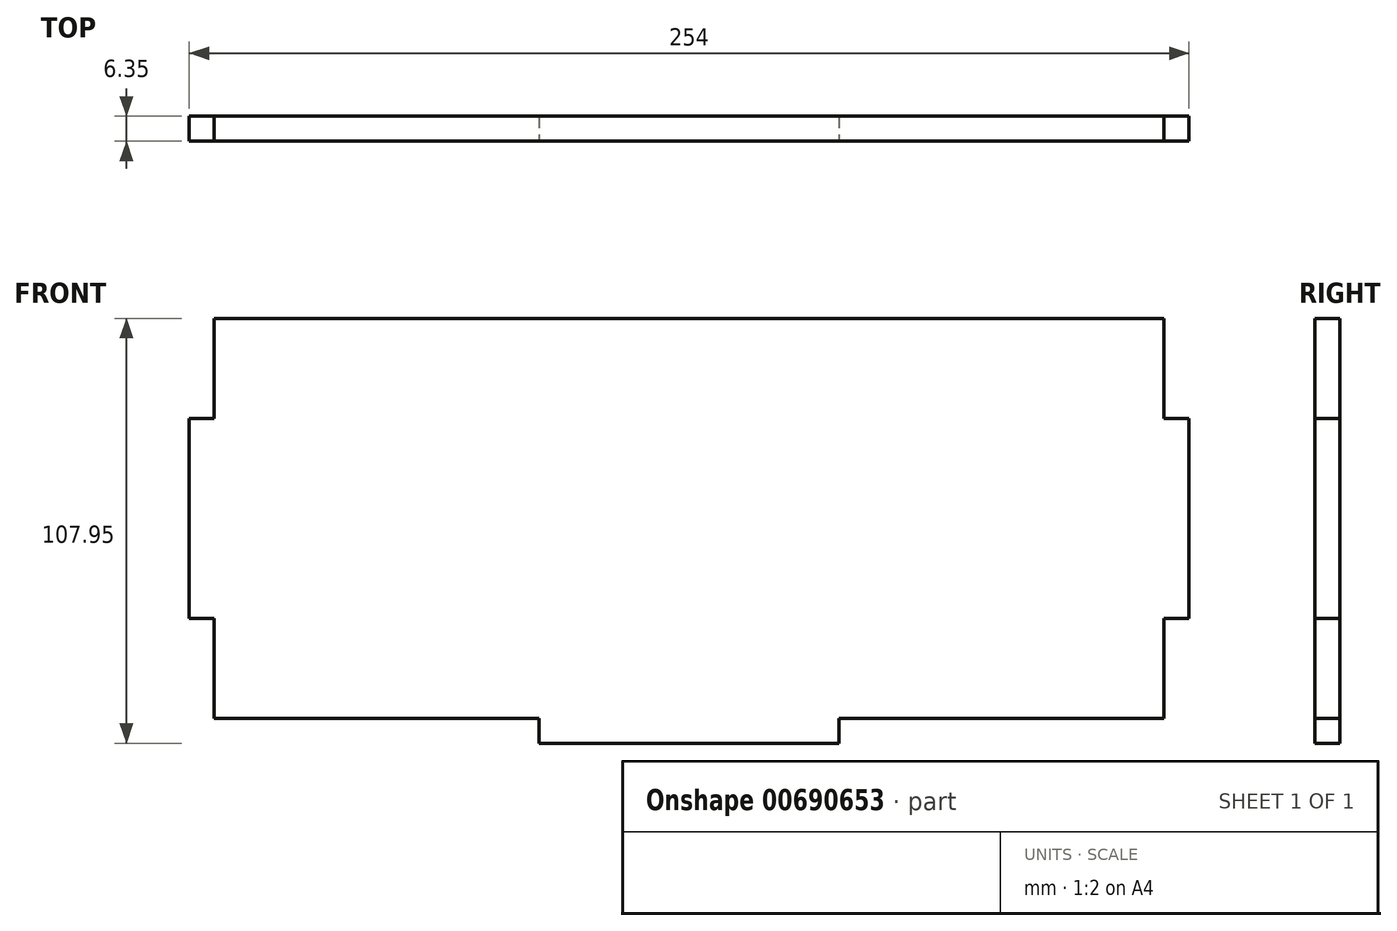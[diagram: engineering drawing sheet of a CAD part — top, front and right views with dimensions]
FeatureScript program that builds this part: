
annotation { "Feature Type Name" : "Feature", "Feature Type Description" : "" }
export const myFeature = defineFeature(function(context is Context, id is Id, definition is map)
    precondition{}
    {
        {
            var Q0;
            Q0=qCreatedBy(makeId("Front.planeOp"),FACE);
            var sketch = newSketch(context, id + "F0", { "sketchPlane" : qUnion([Q0])});
            skLineSegment(sketch, "E0.bottom", {"start": v(-120.65, 101.6) * mm, "end": v(120.65, 101.6) * mm});
            skLineSegment(sketch, "E0.top", {"start": v(-120.65, 0) * mm, "end": v(120.65, 0) * mm});
            skLineSegment(sketch, "E0.left", {"start": v(-120.65, 101.6) * mm, "end": v(-120.65, 0) * mm});
            skLineSegment(sketch, "E0.right", {"start": v(120.65, 101.6) * mm, "end": v(120.65, 0) * mm});
            skSolve(sketch);
        }
        {
            var Q0;
            Q0 = qSketchRegion(id + "F0", true);
            extrude(context, id + "F1", {"entities" : qUnion([Q0]), "depth" : 6.35 * mm, "offsetDistance" : 25.4 * mm});
        }
        {
            var Q0;
            Q0=makeQuery(id+"F1.opExtrude","CAP_FACE",FACE,{"disambiguationData":[OSD([sQuery(id+"F0.wireOp",EDGE,"E0.bottom"),sQuery(id+"F0.wireOp",EDGE,"E0.top"),sQuery(id+"F0.wireOp",EDGE,"E0.left"),sQuery(id+"F0.wireOp",EDGE,"E0.right")])],"isStart":false});
            var sketch = newSketch(context, id + "F2", { "sketchPlane" : qUnion([Q0])});
            skLineSegment(sketch, "E1.bottom", {"start": v(-38.1, 0) * mm, "end": v(38.1, 0) * mm});
            skLineSegment(sketch, "E1.top", {"start": v(-38.1, -6.35) * mm, "end": v(38.1, -6.35) * mm});
            skLineSegment(sketch, "E1.left", {"start": v(-38.1, 0) * mm, "end": v(-38.1, -6.35) * mm});
            skLineSegment(sketch, "E1.right", {"start": v(38.1, 0) * mm, "end": v(38.1, -6.35) * mm});
            skSolve(sketch);
        }
        {
            var Q0;
            Q0 = qSketchRegion(id + "F2", true);
            extrude(context, id + "F3", {"entities" : qUnion([Q0]), "operationType" : NewBodyOperationType.ADD, "oppositeDirection" : true, "depth" : 6.35 * mm, "offsetDistance" : 25.4 * mm});
        }
        {
            var Q0;
            Q0=makeQuery(id+"F3.boolean.opBoolean","MERGE",FACE,{"derivedFrom":[makeQuery(id+"F1.opExtrude","CAP_FACE",FACE,{"disambiguationData":[OSD([sQuery(id+"F0.wireOp",EDGE,"E0.bottom"),sQuery(id+"F0.wireOp",EDGE,"E0.top"),sQuery(id+"F0.wireOp",EDGE,"E0.left"),sQuery(id+"F0.wireOp",EDGE,"E0.right")])],"isStart":false}),makeQuery(id+"F3.opExtrude","CAP_FACE",FACE,{"disambiguationData":[OSD([sQuery(id+"F2.wireOp",EDGE,"E1.bottom"),sQuery(id+"F2.wireOp",EDGE,"E1.top"),sQuery(id+"F2.wireOp",EDGE,"E1.left"),sQuery(id+"F2.wireOp",EDGE,"E1.right")])],"isStart":true})]});
            var sketch = newSketch(context, id + "F4", { "sketchPlane" : qUnion([Q0])});
            skLineSegment(sketch, "E2.bottom", {"start": v(-120.65, 76.2) * mm, "end": v(-127, 76.2) * mm});
            skLineSegment(sketch, "E2.top", {"start": v(-120.65, 25.4) * mm, "end": v(-127, 25.4) * mm});
            skLineSegment(sketch, "E2.left", {"start": v(-120.65, 76.2) * mm, "end": v(-120.65, 25.4) * mm});
            skLineSegment(sketch, "E2.right", {"start": v(-127, 76.2) * mm, "end": v(-127, 25.4) * mm});
            skLineSegment(sketch, "E3.MirrorCS", {"start": v(127, 76.2) * mm, "end": v(127, 25.4) * mm});
            skLineSegment(sketch, "E4.MirrorCS", {"start": v(120.65, 76.2) * mm, "end": v(120.65, 25.4) * mm});
            skLineSegment(sketch, "E5.MirrorCS", {"start": v(120.65, 76.2) * mm, "end": v(127, 76.2) * mm});
            skLineSegment(sketch, "E6.MirrorCS", {"start": v(120.65, 25.4) * mm, "end": v(127, 25.4) * mm});
            skSolve(sketch);
        }
        {
            var Q0;
            Q0 = qSketchRegion(id + "F4", true);
            extrude(context, id + "F5", {"entities" : qUnion([Q0]), "operationType" : NewBodyOperationType.ADD, "oppositeDirection" : true, "depth" : 6.35 * mm, "offsetDistance" : 25.4 * mm});
        }
    });
